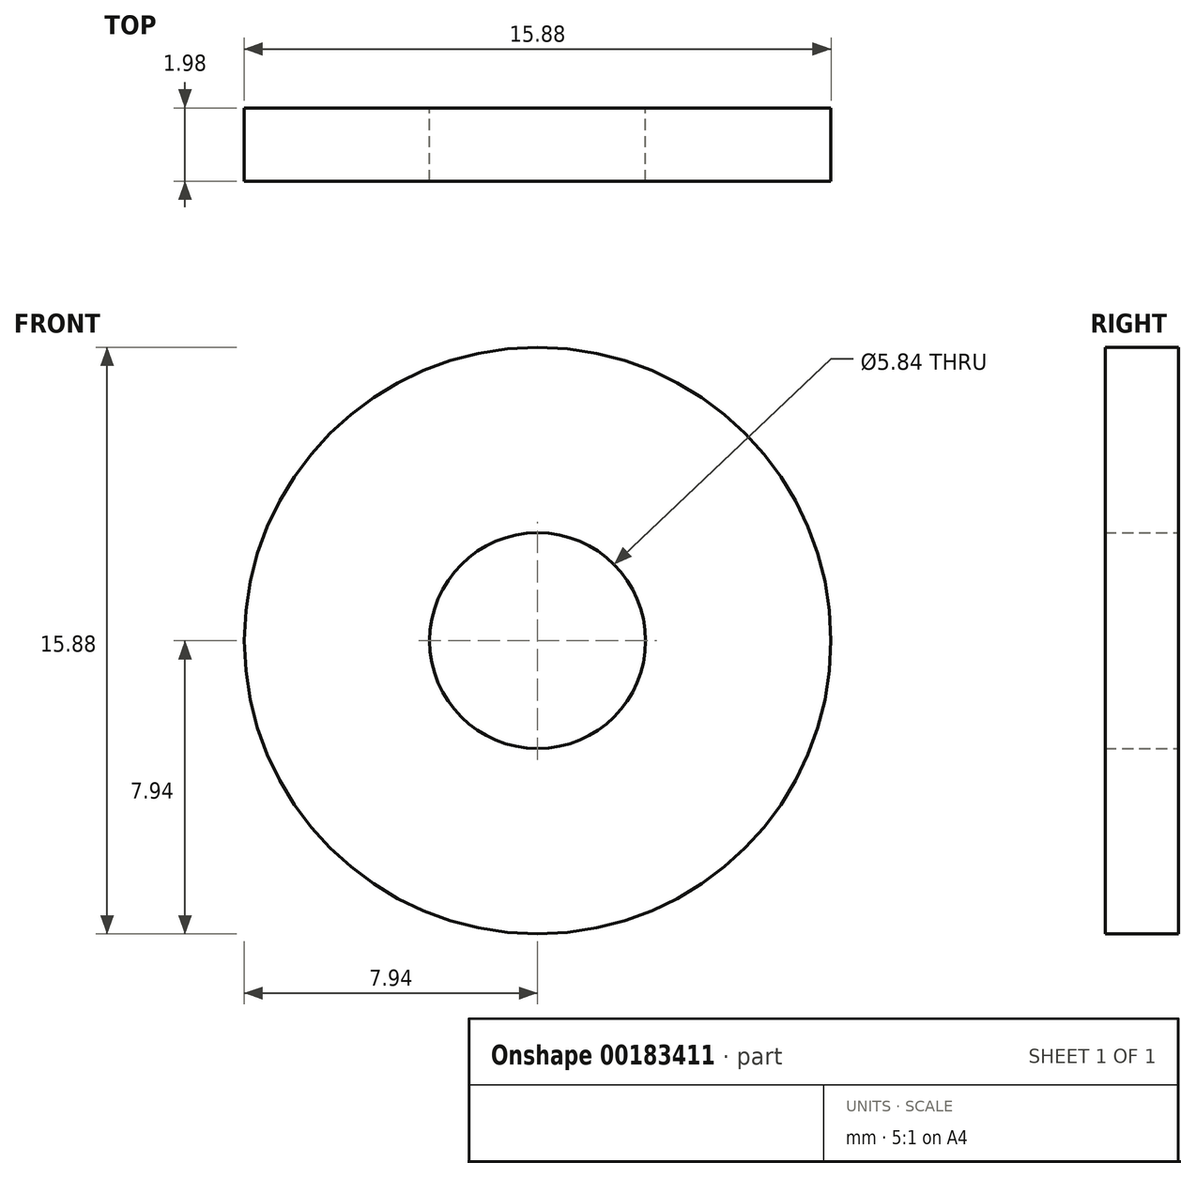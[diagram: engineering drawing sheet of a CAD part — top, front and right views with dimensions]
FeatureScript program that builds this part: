
annotation { "Feature Type Name" : "Feature", "Feature Type Description" : "" }
export const myFeature = defineFeature(function(context is Context, id is Id, definition is map)
    precondition{}
    {
        {
            var Q0;
            Q0=qCreatedBy(makeId("Front.planeOp"),FACE);
            var sketch = newSketch(context, id + "F0", { "sketchPlane" : qUnion([Q0])});
            skCircle(sketch, "E0", {"center": v(0, 0) * mm, "radius": 2.92 * mm});
            skCircle(sketch, "E1", {"center": v(0, 0) * mm, "radius": 7.94 * mm});
            skSolve(sketch);
        }
        {
            var Q0;
            Q0 = qSketchRegion(id + "F0", true);
            extrude(context, id + "F1", {"entities" : qUnion([Q0]), "endBound" : BoundingType.SYMMETRIC, "depth" : 1.98 * mm});
        }
    });
